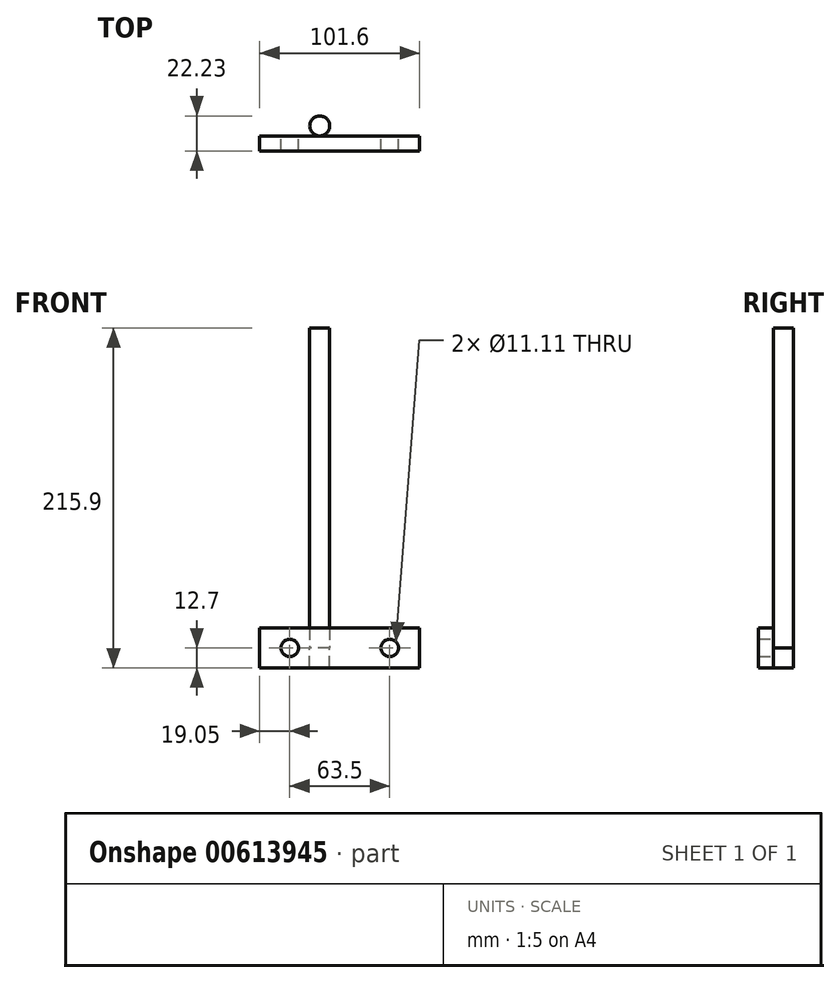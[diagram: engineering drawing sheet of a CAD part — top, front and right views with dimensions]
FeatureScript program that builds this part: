
annotation { "Feature Type Name" : "Feature", "Feature Type Description" : "" }
export const myFeature = defineFeature(function(context is Context, id is Id, definition is map)
    precondition{}
    {
        {
            var Q0;
            Q0=qCreatedBy(makeId("Front.planeOp"),FACE);
            var sketch = newSketch(context, id + "F0", { "sketchPlane" : qUnion([Q0])});
            skLineSegment(sketch, "E0.bottom", {"start": v(50.8, -12.7) * mm, "end": v(-50.8, -12.7) * mm});
            skLineSegment(sketch, "E0.top", {"start": v(50.8, 12.7) * mm, "end": v(-50.8, 12.7) * mm});
            skLineSegment(sketch, "E0.left", {"start": v(50.8, -12.7) * mm, "end": v(50.8, 12.7) * mm});
            skLineSegment(sketch, "E0.right", {"start": v(-50.8, -12.7) * mm, "end": v(-50.8, 12.7) * mm});
            skPoint(sketch, "E0.middle", {"position": v(0, 0) * mm});
            skCircle(sketch, "E1", {"center": v(-31.75, 0) * mm, "radius": 5.56 * mm});
            skCircle(sketch, "E2.MirrorC", {"center": v(31.75, 0) * mm, "radius": 5.56 * mm});
            skSolve(sketch);
        }
        {
            var Q0;
            Q0 = qSketchRegion(id + "F0", true);
            extrude(context, id + "F1", {"entities" : qUnion([Q0]), "depth" : 9.52 * mm, "offsetDistance" : 25.4 * mm});
        }
        {
            var Q0;
            Q0=qCreatedBy(makeId("Top.planeOp"),FACE);
            var sketch = newSketch(context, id + "F2", { "sketchPlane" : qUnion([Q0])});
            skCircle(sketch, "E3", {"center": v(-12.7, 6.35) * mm, "radius": 6.35 * mm});
            skSolve(sketch);
        }
        {
            var Q0;
            Q0=makeQuery(id+"F2.imprint","IMPRINT",FACE,{"disambiguationData":[TD([[makeQuery(id+"F2.imprint","IMPRINT",EDGE,{"derivedFrom":sQuery(id+"F2.wireOp",EDGE,"E3")}),1.0]])]});
            var Q1;
            Q1=sQuery(id+"F2.wireOp",EDGE,"E3");
            extrude(context, id + "F3", {"entities" : qUnion([Q0]), "surfaceEntities" : qUnion([Q1]), "depth" : 203.2 * mm, "offsetDistance" : 25.4 * mm});
        }
        {
            var Q0;
            Q0=makeQuery(id+"F3.opExtrude","CAP_FACE",FACE,{"disambiguationData":[OSD([sQuery(id+"F2.wireOp",EDGE,"E3")])],"isStart":true});
            extrude(context, id + "F4", {"entities" : qUnion([Q0]), "depth" : 12.7 * mm, "offsetDistance" : 25.4 * mm});
        }
    });
